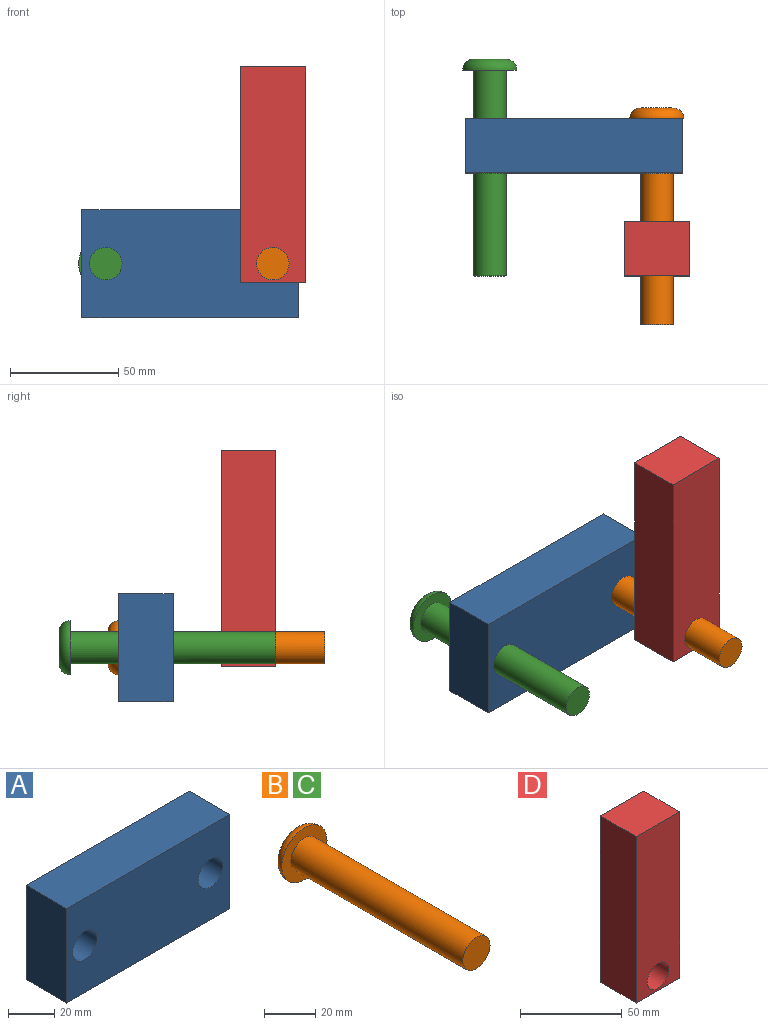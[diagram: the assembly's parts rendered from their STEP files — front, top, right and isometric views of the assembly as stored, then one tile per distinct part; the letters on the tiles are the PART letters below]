
ASSEMBLY  parts=4 mates=4
PART A: 8 faces, bbox 100x25x50 mm
  f0: plane 100x25mm, normal (0,0,1), area 2500mm2, adj f1,f5,f6,f7
  f1: plane 50x25mm, normal (-1,0,0), area 1250mm2, adj f0,f2,f6,f7
  f2: plane 100x25mm, normal (0,0,-1), area 2500mm2, adj f1,f5,f6,f7
  f3: cylinder r=7.5mm len=25mm, axis (0,1,0), area 1178.1mm2, adj f6,f7
  f4: cylinder r=7.5mm len=25mm, axis (0,1,0), area 1178.1mm2, adj f6,f7
  f5: plane 50x25mm, normal (1,0,0), area 1250mm2, adj f0,f2,f6,f7
  f6: plane 100x50mm, normal (0,-1,0), area 4646.6mm2, adj f0,f1,f2,f3,f4,f5
  f7: plane 100x50mm, normal (0,1,0), area 4646.6mm2, adj f0,f1,f2,f3,f4,f5
PART B: 5 faces, bbox 27.1x100x27.1 mm
  f0: cylinder r=7.5mm len=95mm, axis (0,1,0), area 4476.8mm2, adj f1,f2
  f1: plane 15x15mm, normal (0,-1,0), area 176.7mm2, adj f0
  f2: plane 25x25mm, normal (0,-1,0), area 314.2mm2, adj f0,f4
  f3: plane 15x15mm, normal (0,1,0), area 176.7mm2, adj f4
  f4: torus R=7.5mm, axis (0,-1,0), area 527.2mm2, adj f2,f3
PART C: same geometry as B
PART D: 7 faces, bbox 30x25x100 mm
  f0: plane 100x25mm, normal (1,0,0), area 2500mm2, adj f1,f4,f5,f6
  f1: plane 30x25mm, normal (0,0,1), area 750mm2, adj f0,f2,f5,f6
  f2: plane 100x25mm, normal (-1,0,0), area 2500mm2, adj f1,f4,f5,f6
  f3: cylinder r=7.5mm len=25mm, axis (0,1,0), area 1178.1mm2, adj f5,f6
  f4: plane 30x25mm, normal (0,0,-1), area 750mm2, adj f0,f2,f5,f6
  f5: plane 100x30mm, normal (0,-1,0), area 2823.3mm2, adj f0,f1,f2,f3,f4
  f6: plane 100x30mm, normal (0,1,0), area 2823.3mm2, adj f0,f1,f2,f3,f4
PLACE A t=(95.54,-95.51,-12.13)mm
PLACE B t=(78.94,-90.51,-42.89)mm
PLACE C t=(1.88,-68.01,-42.89)mm
PLACE D t=(117.53,-143.01,-57.77)mm
MATE fastened A.f4 <-> C.f0  axis (0,1,0) through (56.53,-95.51,-12.13)mm
MATE revolute D.f3 <-> B.f0  axis (0,1,0) through (133.6,-143.01,-12.13)mm
MATE revolute A.f4 <-> C.f0  axis (0,-1,0) through (56.53,-120.51,-12.13)mm
MATE revolute B.f0 <-> A.f3  axis (0,-1,0) through (133.6,-95.51,-12.13)mm
